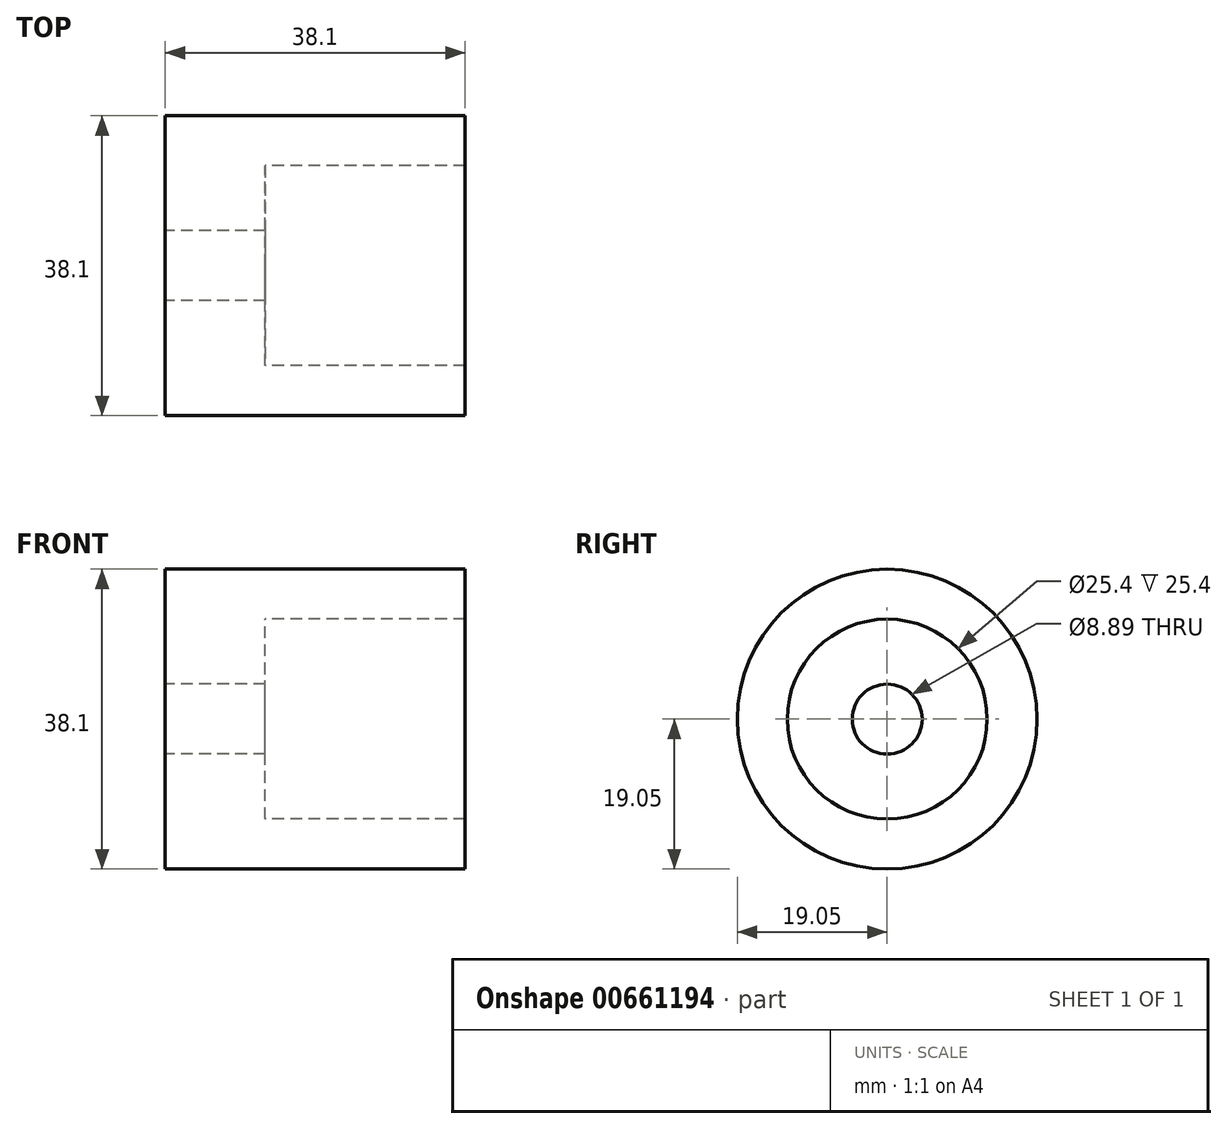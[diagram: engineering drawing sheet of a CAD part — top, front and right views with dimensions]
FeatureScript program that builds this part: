
annotation { "Feature Type Name" : "Feature", "Feature Type Description" : "" }
export const myFeature = defineFeature(function(context is Context, id is Id, definition is map)
    precondition{}
    {
        {
            var Q0;
            Q0=qCreatedBy(makeId("Right.planeOp"),FACE);
            var sketch = newSketch(context, id + "F0", { "sketchPlane" : qUnion([Q0])});
            skCircle(sketch, "E0", {"center": v(0, 0) * mm, "radius": 19.05 * mm});
            skCircle(sketch, "E1", {"center": v(0, 0) * mm, "radius": 12.7 * mm});
            skCircle(sketch, "E2", {"center": v(0, 0) * mm, "radius": 4.45 * mm});
            skSolve(sketch);
        }
        {
            var Q0;
            Q0=makeQuery(id+"F0.imprint","IMPRINT",FACE,{"disambiguationData":[TD([[makeQuery(id+"F0.imprint","IMPRINT",EDGE,{"derivedFrom":sQuery(id+"F0.wireOp",EDGE,"E0")}),1.0]])]});
            extrude(context, id + "F1", {"entities" : qUnion([Q0]), "depth" : 38.1 * mm, "offsetDistance" : 25.4 * mm});
        }
        {
            var Q0;
            Q0=makeQuery(id+"F0.imprint","IMPRINT",FACE,{"disambiguationData":[TD([[makeQuery(id+"F0.imprint","IMPRINT",EDGE,{"derivedFrom":sQuery(id+"F0.wireOp",EDGE,"E1")}),1.0]])]});
            extrude(context, id + "F2", {"entities" : qUnion([Q0]), "operationType" : NewBodyOperationType.ADD, "depth" : 12.7 * mm, "offsetDistance" : 25.4 * mm});
        }
    });
